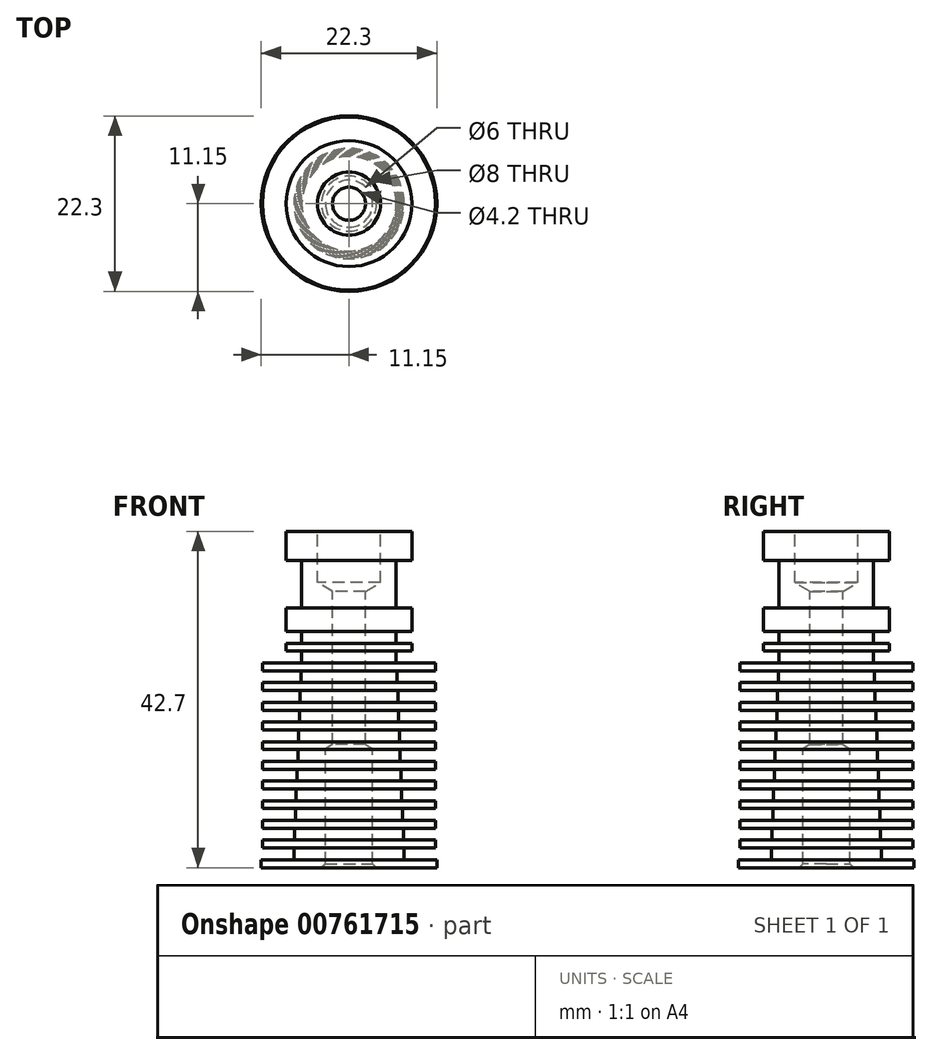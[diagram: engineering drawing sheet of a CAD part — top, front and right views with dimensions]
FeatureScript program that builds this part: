
annotation { "Feature Type Name" : "Feature", "Feature Type Description" : "" }
export const myFeature = defineFeature(function(context is Context, id is Id, definition is map)
    precondition{}
    {
        {
            var Q0;
            Q0=qCreatedBy(makeId("Front.planeOp"),FACE);
            var sketch = newSketch(context, id + "F0", { "sketchPlane" : qUnion([Q0])});
            skLineSegment(sketch, "E0", {"start": v(0, 0) * mm, "end": v(0, 42.7) * mm});
            skLineSegment(sketch, "E1", {"start": v(0, 42.7) * mm, "end": v(8, 42.7) * mm});
            skLineSegment(sketch, "E2", {"start": v(11.15, 1) * mm, "end": v(11.15, 0) * mm});
            skLineSegment(sketch, "E3", {"start": v(11.15, 0) * mm, "end": v(0, 0) * mm});
            skLineSegment(sketch, "E4", {"start": v(8, 42.7) * mm, "end": v(8, 26) * mm});
            skLineSegment(sketch, "E5", {"start": v(8, 26) * mm, "end": v(11, 26) * mm});
            skLineSegment(sketch, "E6", {"start": v(11.15, 1) * mm, "end": v(11, 1) * mm});
            skLineSegment(sketch, "E7", {"start": v(11, 1) * mm, "end": v(11, 26) * mm});
            skLineSegment(sketch, "E8.MirrorCS", {"start": v(-11.15, 1) * mm, "end": v(-11.15, 0) * mm, "construction": true});
            skLineSegment(sketch, "E9.MirrorCS", {"start": v(-8, 42.7) * mm, "end": v(-8, 26) * mm, "construction": true});
            skLineSegment(sketch, "E10.MirrorCS", {"start": v(-11, 1) * mm, "end": v(-11, 26) * mm, "construction": true});
            skSolve(sketch);
        }
        {
            var Q0;
            Q0 = qSketchRegion(id + "F0", true);
            var Q1;
            Q1=sQuery(id+"F0.wireOp",EDGE,"E0");
            revolve(context, id + "F1", {"surfaceOperationType" : NewSurfaceOperationType.NEW, "entities" : qUnion([Q0]), "axis" : qUnion([Q1]), "revolveType" : RevolveType.FULL});
        }
        {
            var Q0;
            Q0=qCreatedBy(makeId("Front.planeOp"),FACE);
            var sketch = newSketch(context, id + "F2", { "sketchPlane" : qUnion([Q0])});
            skLineSegment(sketch, "E11", {"start": v(11, 39) * mm, "end": v(6, 39) * mm});
            skLineSegment(sketch, "E12", {"start": v(6, 33) * mm, "end": v(11, 33) * mm});
            skLineSegment(sketch, "E13", {"start": v(6, 39) * mm, "end": v(6, 33) * mm});
            skLineSegment(sketch, "E14", {"start": v(11, 39) * mm, "end": v(11, 33) * mm});
            skLineSegment(sketch, "E15.bottom", {"start": v(0, 0) * mm, "end": v(0, 0) * mm});
            skLineSegment(sketch, "E15.top", {"start": v(0, 45) * mm, "end": v(0, 45) * mm});
            skLineSegment(sketch, "E15.left", {"start": v(0, 0) * mm, "end": v(0, 45) * mm});
            skLineSegment(sketch, "E15.right", {"start": v(0, 0) * mm, "end": v(0, 45) * mm});
            skLineSegment(sketch, "E16.MirrorCS", {"start": v(-6, 39) * mm, "end": v(-6, 33) * mm, "construction": true});
            skLineSegment(sketch, "E17.bottom", {"start": v(11, 30) * mm, "end": v(6, 30) * mm});
            skLineSegment(sketch, "E17.top", {"start": v(11, 28.5) * mm, "end": v(6, 28.5) * mm});
            skLineSegment(sketch, "E17.left", {"start": v(11, 30) * mm, "end": v(11, 28.5) * mm});
            skLineSegment(sketch, "E17.right", {"start": v(6, 30) * mm, "end": v(6, 28.5) * mm});
            skLineSegment(sketch, "E18.bottom", {"start": v(11, 27.5) * mm, "end": v(6, 27.5) * mm});
            skLineSegment(sketch, "E18.top", {"start": v(11, 26) * mm, "end": v(6, 26) * mm});
            skLineSegment(sketch, "E18.left", {"start": v(11, 27.5) * mm, "end": v(11, 26) * mm});
            skLineSegment(sketch, "E18.right", {"start": v(6, 27.5) * mm, "end": v(6, 26) * mm});
            skSolve(sketch);
        }
        {
            var Q0;
            Q0 = qSketchRegion(id + "F2", true);
            var Q1;
            Q1=sQuery(id+"F2.wireOp",EDGE,"E15.right");
            revolve(context, id + "F3", {"operationType" : NewBodyOperationType.REMOVE, "surfaceOperationType" : NewSurfaceOperationType.NEW, "entities" : qUnion([Q0]), "axis" : qUnion([Q1]), "revolveType" : RevolveType.FULL, "oppositeDirection" : true});
        }
        {
            var Q0;
            Q0=qCreatedBy(makeId("Front.planeOp"),FACE);
            var sketch = newSketch(context, id + "F4", { "sketchPlane" : qUnion([Q0])});
            skLineSegment(sketch, "E19.bottom", {"start": v(15, 2.5) * mm, "end": v(7, 2.5) * mm});
            skLineSegment(sketch, "E19.top", {"start": v(15, 1) * mm, "end": v(7, 1) * mm});
            skLineSegment(sketch, "E19.left", {"start": v(15, 2.5) * mm, "end": v(15, 1) * mm});
            skLineSegment(sketch, "E19.right", {"start": v(7, 2.5) * mm, "end": v(7, 1) * mm});
            skLineSegment(sketch, "E20.bottom", {"start": v(15, 5) * mm, "end": v(6.9, 5) * mm});
            skLineSegment(sketch, "E20.top", {"start": v(15, 3.5) * mm, "end": v(6.9, 3.5) * mm});
            skLineSegment(sketch, "E20.left", {"start": v(15, 5) * mm, "end": v(15, 3.5) * mm});
            skLineSegment(sketch, "E20.right", {"start": v(6.9, 5) * mm, "end": v(6.9, 3.5) * mm});
            skLineSegment(sketch, "E21.bottom", {"start": v(15, 7.5) * mm, "end": v(6.8, 7.5) * mm});
            skLineSegment(sketch, "E21.top", {"start": v(15, 6) * mm, "end": v(6.8, 6) * mm});
            skLineSegment(sketch, "E21.left", {"start": v(15, 7.5) * mm, "end": v(15, 6) * mm});
            skLineSegment(sketch, "E21.right", {"start": v(6.8, 7.5) * mm, "end": v(6.8, 6) * mm});
            skLineSegment(sketch, "E22.bottom", {"start": v(15, 10) * mm, "end": v(6.7, 10) * mm});
            skLineSegment(sketch, "E22.top", {"start": v(15, 8.5) * mm, "end": v(6.7, 8.5) * mm});
            skLineSegment(sketch, "E22.left", {"start": v(15, 10) * mm, "end": v(15, 8.5) * mm});
            skLineSegment(sketch, "E22.right", {"start": v(6.7, 10) * mm, "end": v(6.7, 8.5) * mm});
            skLineSegment(sketch, "E23.bottom", {"start": v(15, 12.5) * mm, "end": v(6.6, 12.5) * mm});
            skLineSegment(sketch, "E23.top", {"start": v(15, 11) * mm, "end": v(6.6, 11) * mm});
            skLineSegment(sketch, "E23.left", {"start": v(15, 12.5) * mm, "end": v(15, 11) * mm});
            skLineSegment(sketch, "E23.right", {"start": v(6.6, 12.5) * mm, "end": v(6.6, 11) * mm});
            skLineSegment(sketch, "E24.bottom", {"start": v(15, 15) * mm, "end": v(6.5, 15) * mm});
            skLineSegment(sketch, "E24.top", {"start": v(15, 13.5) * mm, "end": v(6.5, 13.5) * mm});
            skLineSegment(sketch, "E24.left", {"start": v(15, 15) * mm, "end": v(15, 13.5) * mm});
            skLineSegment(sketch, "E24.right", {"start": v(6.5, 15) * mm, "end": v(6.5, 13.5) * mm});
            skLineSegment(sketch, "E25.bottom", {"start": v(15, 17.5) * mm, "end": v(6.4, 17.5) * mm});
            skLineSegment(sketch, "E25.top", {"start": v(15, 16) * mm, "end": v(6.4, 16) * mm});
            skLineSegment(sketch, "E25.left", {"start": v(15, 17.5) * mm, "end": v(15, 16) * mm});
            skLineSegment(sketch, "E25.right", {"start": v(6.4, 17.5) * mm, "end": v(6.4, 16) * mm});
            skLineSegment(sketch, "E26.bottom", {"start": v(15, 20) * mm, "end": v(6.3, 20) * mm});
            skLineSegment(sketch, "E26.top", {"start": v(15, 18.5) * mm, "end": v(6.3, 18.5) * mm});
            skLineSegment(sketch, "E26.left", {"start": v(15, 20) * mm, "end": v(15, 18.5) * mm});
            skLineSegment(sketch, "E26.right", {"start": v(6.3, 20) * mm, "end": v(6.3, 18.5) * mm});
            skLineSegment(sketch, "E27.bottom", {"start": v(15, 22.5) * mm, "end": v(6.2, 22.5) * mm});
            skLineSegment(sketch, "E27.top", {"start": v(15, 21) * mm, "end": v(6.2, 21) * mm});
            skLineSegment(sketch, "E27.left", {"start": v(15, 22.5) * mm, "end": v(15, 21) * mm});
            skLineSegment(sketch, "E27.right", {"start": v(6.2, 22.5) * mm, "end": v(6.2, 21) * mm});
            skLineSegment(sketch, "E28.bottom", {"start": v(15, 25) * mm, "end": v(6.1, 25) * mm});
            skLineSegment(sketch, "E28.top", {"start": v(15, 23.5) * mm, "end": v(6.1, 23.5) * mm});
            skLineSegment(sketch, "E28.left", {"start": v(15, 25) * mm, "end": v(15, 23.5) * mm});
            skLineSegment(sketch, "E28.right", {"start": v(6.1, 25) * mm, "end": v(6.1, 23.5) * mm});
            skLineSegment(sketch, "E29", {"start": v(0, 0) * mm, "end": v(0, 26.18) * mm, "construction": true});
            skLineSegment(sketch, "E30.MirrorCS", {"start": v(-6.1, 25) * mm, "end": v(-6.1, 23.5) * mm});
            skLineSegment(sketch, "E31.MirrorCS", {"start": v(-6.2, 22.5) * mm, "end": v(-6.2, 21) * mm});
            skLineSegment(sketch, "E32.MirrorCS", {"start": v(-6.3, 20) * mm, "end": v(-6.3, 18.5) * mm});
            skLineSegment(sketch, "E33.MirrorCS", {"start": v(-6.4, 17.5) * mm, "end": v(-6.4, 16) * mm});
            skLineSegment(sketch, "E34.MirrorCS", {"start": v(-6.5, 15) * mm, "end": v(-6.5, 13.5) * mm});
            skLineSegment(sketch, "E35.MirrorCS", {"start": v(-6.6, 12.5) * mm, "end": v(-6.6, 11) * mm});
            skLineSegment(sketch, "E36.MirrorCS", {"start": v(-6.7, 10) * mm, "end": v(-6.7, 8.5) * mm});
            skLineSegment(sketch, "E37.MirrorCS", {"start": v(-6.8, 7.5) * mm, "end": v(-6.8, 6) * mm});
            skLineSegment(sketch, "E38.MirrorCS", {"start": v(-6.9, 5) * mm, "end": v(-6.9, 3.5) * mm});
            skLineSegment(sketch, "E39.MirrorCS", {"start": v(-7, 2.5) * mm, "end": v(-7, 1) * mm});
            skSolve(sketch);
        }
        {
            var Q0;
            Q0 = qSketchRegion(id + "F4", true);
            var Q1;
            Q1=sQuery(id+"F4.wireOp",EDGE,"E29");
            revolve(context, id + "F5", {"operationType" : NewBodyOperationType.REMOVE, "surfaceOperationType" : NewSurfaceOperationType.NEW, "entities" : qUnion([Q0]), "axis" : qUnion([Q1]), "revolveType" : RevolveType.FULL, "oppositeDirection" : true});
        }
        {
            var Q0;
            Q0=qCreatedBy(makeId("Front.planeOp"),FACE);
            var sketch = newSketch(context, id + "F6", { "sketchPlane" : qUnion([Q0])});
            skLineSegment(sketch, "E40", {"start": v(0, 0) * mm, "end": v(0, 42.7) * mm});
            skLineSegment(sketch, "E41", {"start": v(4, 42.7) * mm, "end": v(4, 36.2) * mm});
            skLineSegment(sketch, "E42", {"start": v(4, 36.2) * mm, "end": v(2.1, 35.06) * mm});
            skLineSegment(sketch, "E43", {"start": v(2.1, 35.06) * mm, "end": v(2.1, 15.64) * mm});
            skLineSegment(sketch, "E44", {"start": v(2.1, 15.64) * mm, "end": v(3, 15.1) * mm});
            skLineSegment(sketch, "E45", {"start": v(3, 15.1) * mm, "end": v(3, 0) * mm});
            skLineSegment(sketch, "E46", {"start": v(3, 0) * mm, "end": v(0, 0) * mm});
            skLineSegment(sketch, "E47", {"start": v(0, 42.7) * mm, "end": v(4, 42.7) * mm});
            skLineSegment(sketch, "E48.MirrorCS", {"start": v(-4, 42.7) * mm, "end": v(-4, 36.2) * mm, "construction": true});
            skLineSegment(sketch, "E49.MirrorCS", {"start": v(-2.1, 35.06) * mm, "end": v(-2.1, 15.64) * mm, "construction": true});
            skLineSegment(sketch, "E50.MirrorCS", {"start": v(-4, 36.2) * mm, "end": v(-2.1, 35.06) * mm, "construction": true});
            skLineSegment(sketch, "E51.MirrorCS", {"start": v(-2.1, 15.64) * mm, "end": v(-3, 15.1) * mm, "construction": true});
            skLineSegment(sketch, "E52.MirrorCS", {"start": v(-3, 15.1) * mm, "end": v(-3, 0) * mm, "construction": true});
            skSolve(sketch);
        }
        {
            var Q0;
            Q0 = qSketchRegion(id + "F6", true);
            var Q1;
            Q1=sQuery(id+"F6.wireOp",EDGE,"E40");
            revolve(context, id + "F7", {"operationType" : NewBodyOperationType.REMOVE, "surfaceOperationType" : NewSurfaceOperationType.NEW, "entities" : qUnion([Q0]), "axis" : qUnion([Q1]), "revolveType" : RevolveType.FULL, "oppositeDirection" : true});
        }
        {
            var Q0;
            Q0=qCreatedBy(makeId("Top.planeOp"),FACE);
            var sketch = newSketch(context, id + "F8", { "sketchPlane" : qUnion([Q0])});
            skPoint(sketch, "E53", {"position": v(0, 0) * mm});
            skSolve(sketch);
        }
        {
            var Q0;
            Q0=sQuery(id+"F8.wireOp",VERTEX,"E53");
            var Q1;
            Q1=makeQuery(id+"F1.opRevolve","SWEPT_BODY",BODY,{"disambiguationData":[OSD([sQuery(id+"F0.wireOp",EDGE,"E0"),sQuery(id+"F0.wireOp",EDGE,"E1"),sQuery(id+"F0.wireOp",EDGE,"E2"),sQuery(id+"F0.wireOp",EDGE,"E3"),sQuery(id+"F0.wireOp",EDGE,"E4"),sQuery(id+"F0.wireOp",EDGE,"E5"),sQuery(id+"F0.wireOp",EDGE,"E6"),sQuery(id+"F0.wireOp",EDGE,"E7")])]});
            hole(context, id + "F9", {"style" : HoleStyle.C_SINK, "endStyle" : HoleEndStyle.BLIND, "oppositeDirection" : true, "holeDiameter" : 6 * mm, "cSinkDiameter" : 7 * mm, "cSinkAngle" : 90 * degree, "majorDiameter" : 5 * mm, "holeDepth" : 10 * mm, "isTappedThrough" : true, "tappedDepth" : 12 * mm, "tapClearance" : 3, "locations" : qUnion([Q0]), "scope" : qUnion([Q1])});
        }
    });
